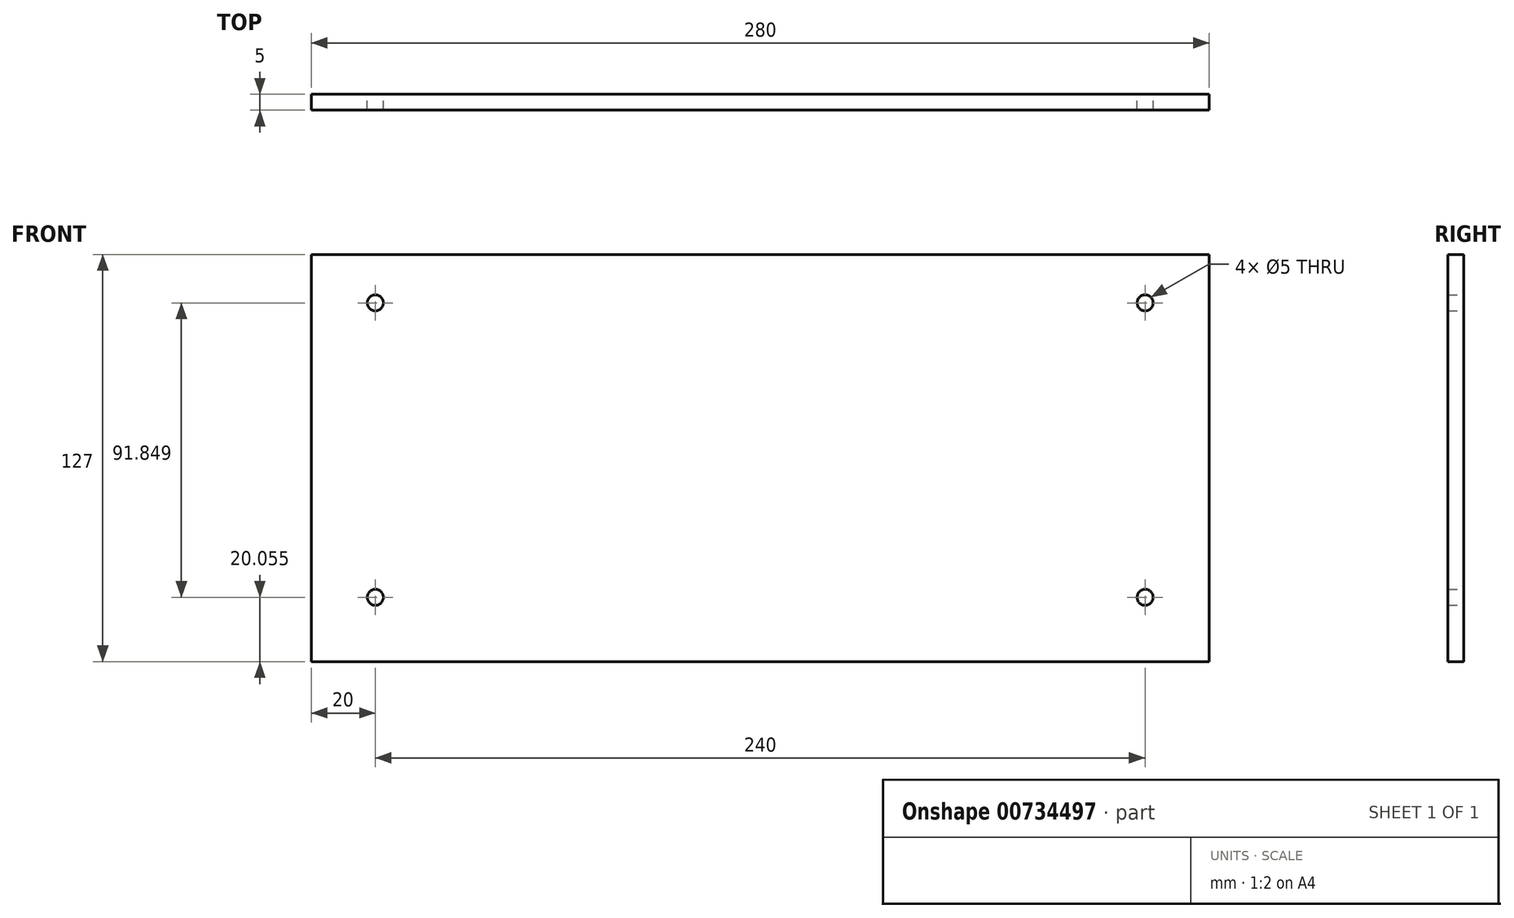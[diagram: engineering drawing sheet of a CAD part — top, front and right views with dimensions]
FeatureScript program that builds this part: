
annotation { "Feature Type Name" : "Feature", "Feature Type Description" : "" }
export const myFeature = defineFeature(function(context is Context, id is Id, definition is map)
    precondition{}
    {
        {
            var Q0;
            Q0=qCreatedBy(makeId("Front.planeOp"),FACE);
            var sketch = newSketch(context, id + "F0", { "sketchPlane" : qUnion([Q0])});
            skLineSegment(sketch, "E0.bottom", {"start": v(0, 0) * mm, "end": v(-280, 0) * mm});
            skLineSegment(sketch, "E0.top", {"start": v(0, 127) * mm, "end": v(-280, 127) * mm});
            skLineSegment(sketch, "E0.left", {"start": v(0, 0) * mm, "end": v(0, 127) * mm});
            skLineSegment(sketch, "E0.right", {"start": v(-280, 0) * mm, "end": v(-280, 127) * mm});
            skCircle(sketch, "E1", {"center": v(-260, 111.9) * mm, "radius": 2.5 * mm});
            skCircle(sketch, "E2", {"center": v(-260, 20.06) * mm, "radius": 2.5 * mm});
            skCircle(sketch, "E3", {"center": v(-20, 111.9) * mm, "radius": 2.5 * mm});
            skCircle(sketch, "E4", {"center": v(-20, 20.06) * mm, "radius": 2.5 * mm});
            skSolve(sketch);
        }
        {
            var Q0;
            Q0=makeQuery(id+"F0.imprint","IMPRINT",FACE,{"disambiguationData":[TD([[makeQuery(id+"F0.imprint","IMPRINT",EDGE,{"derivedFrom":sQuery(id+"F0.wireOp",EDGE,"E0.bottom")}),-1.0]])]});
            extrude(context, id + "F1", {"entities" : qUnion([Q0]), "depth" : 5 * mm, "offsetDistance" : 25 * mm});
        }
    });
